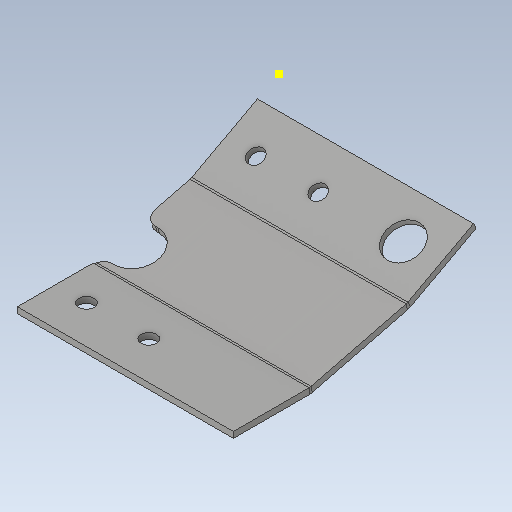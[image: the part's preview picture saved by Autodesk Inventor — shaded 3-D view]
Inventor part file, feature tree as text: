
AUTODESK INVENTOR PART (.ipt)
format: ipt  version: 2020.1 (Build 241239000, 239)  size: 275,456 bytes
history: native  units: mm
features: other x8, sketch x7, sheet_metal_op x3, hole x3, reference x2, plane x1, fillet x1, projected_geometry x1
ambient origin geometry x8: Origin, YZ Plane, XZ Plane, XY Plane, X Axis, Y Axis, Z Axis, Center Point
bodies: Body1 (feature_tree)
feature tree (26):
  other  "model.ipt"
  plane  "Work Plane1"
  sketch  "Sketch2"  dims[d7=10.0mm d9=5.0mm]
  sheet_metal_op  "Contour Flange1"
  hole  "Hole1"  [1 undecoded]
  hole  "Hole7"  [1 undecoded]
  hole  "Hole8"  [1 undecoded]
  sketch  "Sketch11"  dims[d17=20.0mm]
  fillet  "Fillet1"  Radius=180.0mm
  other  "Plate3"
  sheet_metal_op  "Bend2"
  sheet_metal_op  "Corner1"
  sketch  "Sketch7"  dims[d10=5.0mm d11=2.5mm]
  sketch  "Sketch8"  dims[d12=10.0mm d13=6.25mm d14=180.0mm]
  sketch  "Sketch9"  dims[d15=6.25mm]
  sketch  "Sketch10"  dims[d16=5.0mm]
  reference  "Reference1"
  reference  "Reference2"
  sketch  "Sketch12"  dims[d18=5.0mm d19=6.25mm d20=39.0mm d21=39.0mm d22=13.0mm d23=6.0mm d24=4.0mm d25=2.0mm d26=90.0deg d27=5.0mm d28=20.594885mm d74=62.052154mm d75=31.026077mm d76=26.0mm d77=52.0mm d78=81.718239mm d79=40.85912mm d80=26.0mm d81=52.0mm d82=13.0mm d83=6.0mm d84=4.0mm d85=2.0mm d86=90.0deg d87=5.0mm d88=20.594885mm d89=63.10912mm d90=31.55456mm d91=26.0mm d92=52.0mm d93=13.0mm d94=6.0mm d95=4.0mm d96=2.0mm d97=90.0deg d98=5.0mm d99=20.594885mm d100=20.0mm d101=20.0mm d102=302.737mm d103=30.0mm d104=302.737mm d105=5.0mm d106=0.0mm d107=18.5mm d108=30.0mm d109=62.052154mm d110=31.026077mm d111=31.026077mm d112=5.0mm d113=0.0mm d114=10.0mm d29=1.0mm d30=1.0mm]
  projected_geometry  "Projected Loop1"
  other  "Cut1"
  other  "Cut2"
  parser-record x1  (decoder bookkeeping rows leaked as tree rows — omitted from the tree; the rows remain in map.json)
  other  "modul.iam"
  other  "vange:1"
  other  "Definition1"
note: 3 required parameter values undecoded (feature->parameter linkage not recoverable at this tier; creation-order binding heuristic only, values carry confidence <= 0.55)
note: 1 file-system path scrubbed to <path> (originals preserved in map.json)
